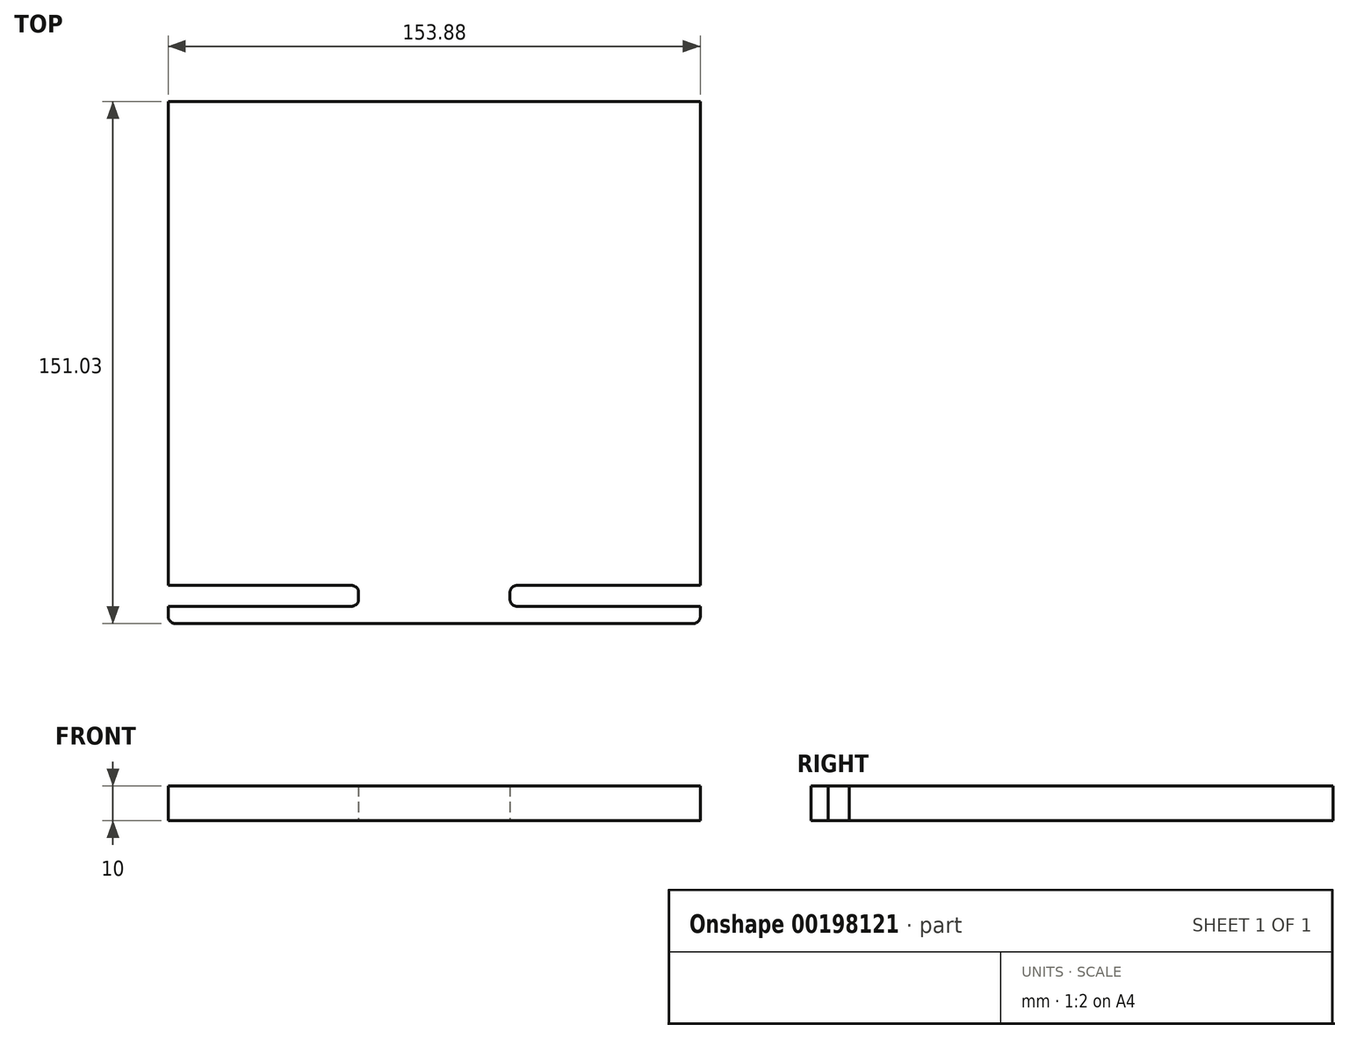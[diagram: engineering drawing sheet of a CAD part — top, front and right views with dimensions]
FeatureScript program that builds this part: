
annotation { "Feature Type Name" : "Feature", "Feature Type Description" : "" }
export const myFeature = defineFeature(function(context is Context, id is Id, definition is map)
    precondition{}
    {
        {
            var Q0;
            Q0=qCreatedBy(makeId("Top.planeOp"),FACE);
            var sketch = newSketch(context, id + "F0", { "sketchPlane" : qUnion([Q0])});
            skLineSegment(sketch, "E0.top", {"start": v(-76.94, -107.5) * mm, "end": v(76.94, -107.5) * mm});
            skPoint(sketch, "E0.middle", {"position": v(0, 0) * mm});
            skLineSegment(sketch, "E1.bottom", {"start": v(23.9, -119.03) * mm, "end": v(76.94, -119.03) * mm});
            skLineSegment(sketch, "E1.top", {"start": v(23.9, -113) * mm, "end": v(76.94, -113) * mm});
            skPoint(sketch, "E1.middle", {"position": v(38.5, -116.01) * mm});
            skLineSegment(sketch, "E2.bottom", {"start": v(-76.94, -119.03) * mm, "end": v(-23.9, -119.03) * mm});
            skLineSegment(sketch, "E2.top", {"start": v(-76.94, -113) * mm, "end": v(-23.9, -113) * mm});
            skPoint(sketch, "E2.middle", {"position": v(-38.49, -116.02) * mm});
            skLineSegment(sketch, "E3", {"start": v(-76.94, -107.5) * mm, "end": v(-76.94, -113) * mm});
            skLineSegment(sketch, "E4", {"start": v(-0.04, -113) * mm, "end": v(0.04, -113) * mm});
            skLineSegment(sketch, "E5", {"start": v(-0.04, -119.03) * mm, "end": v(0.04, -119.03) * mm});
            skLineSegment(sketch, "E6", {"start": v(0, -113) * mm, "end": v(0, -119.03) * mm});
            skPoint(sketch, "E6.startSnap0", {"position": v(0, -113) * mm});
            skLineSegment(sketch, "E7.0", {"start": v(-21.9, -115) * mm, "end": v(-21.9, -117.03) * mm});
            skLineSegment(sketch, "E8.0", {"start": v(21.9, -115) * mm, "end": v(21.9, -117.03) * mm});
            skLineSegment(sketch, "E9", {"start": v(76.94, -107.5) * mm, "end": v(76.94, -113) * mm});
            skPoint(sketch, "E10.newPointA", {"position": v(-0.04, -113) * mm});
            skArc(sketch, "E10.filletArc", {"start": v(-21.9, -115) * mm, "mid": v(-22.49, -113.6) * mm, "end": v(-23.9, -113) * mm});
            skPoint(sketch, "E11.newPointB", {"position": v(0.04, -113) * mm});
            skArc(sketch, "E11.filletArc", {"start": v(23.9, -113) * mm, "mid": v(22.49, -113.58) * mm, "end": v(21.9, -115) * mm});
            skLineSegment(sketch, "E12", {"start": v(-76.94, -119.03) * mm, "end": v(-76.94, -122.03) * mm});
            skLineSegment(sketch, "E13", {"start": v(76.94, -119.03) * mm, "end": v(76.94, -122.03) * mm});
            skLineSegment(sketch, "E14", {"start": v(-74.94, -124.03) * mm, "end": v(74.94, -124.03) * mm});
            skPoint(sketch, "E15.newPointB", {"position": v(0.04, -119.03) * mm});
            skArc(sketch, "E15.filletArc", {"start": v(21.9, -117.03) * mm, "mid": v(22.49, -118.44) * mm, "end": v(23.9, -119.03) * mm});
            skPoint(sketch, "E16.newPointA", {"position": v(-0.04, -119.03) * mm});
            skArc(sketch, "E16.filletArc", {"start": v(-23.9, -119.03) * mm, "mid": v(-22.49, -118.44) * mm, "end": v(-21.9, -117.03) * mm});
            skPoint(sketch, "E17.visualSharp", {"position": v(-76.94, -124.03) * mm});
            skArc(sketch, "E17.filletArc", {"start": v(-76.94, -122.03) * mm, "mid": v(-76.35, -123.44) * mm, "end": v(-74.94, -124.03) * mm});
            skPoint(sketch, "E18.visualSharp", {"position": v(76.94, -124.03) * mm});
            skArc(sketch, "E18.filletArc", {"start": v(74.94, -124.03) * mm, "mid": v(76.35, -123.44) * mm, "end": v(76.94, -122.03) * mm});
            skLineSegment(sketch, "E19.top", {"start": v(-76.94, 27) * mm, "end": v(76.94, 27) * mm});
            skLineSegment(sketch, "E19.left", {"start": v(-76.94, -107.5) * mm, "end": v(-76.94, 27) * mm});
            skLineSegment(sketch, "E19.right", {"start": v(76.94, -107.5) * mm, "end": v(76.94, 27) * mm});
            skSolve(sketch);
        }
        {
            var Q0;
            Q0=makeQuery(id+"F0.imprint","IMPRINT",FACE,{"disambiguationData":[TD([[makeQuery(id+"F0.imprint","IMPRINT",EDGE,{"derivedFrom":sQuery(id+"F0.wireOp",EDGE,"E0.top")}),1.0]])]});
            var Q1;
            Q1=makeQuery(id+"F0.imprint","IMPRINT",FACE,{"disambiguationData":[TD([[makeQuery(id+"F0.imprint","IMPRINT",EDGE,{"derivedFrom":sQuery(id+"F0.wireOp",EDGE,"E1.bottom")}),-1.0]])]});
            extrude(context, id + "F1", {"entities" : qUnion([Q0, Q1]), "endBound" : BoundingType.SYMMETRIC, "depth" : 10 * mm});
        }
    });
